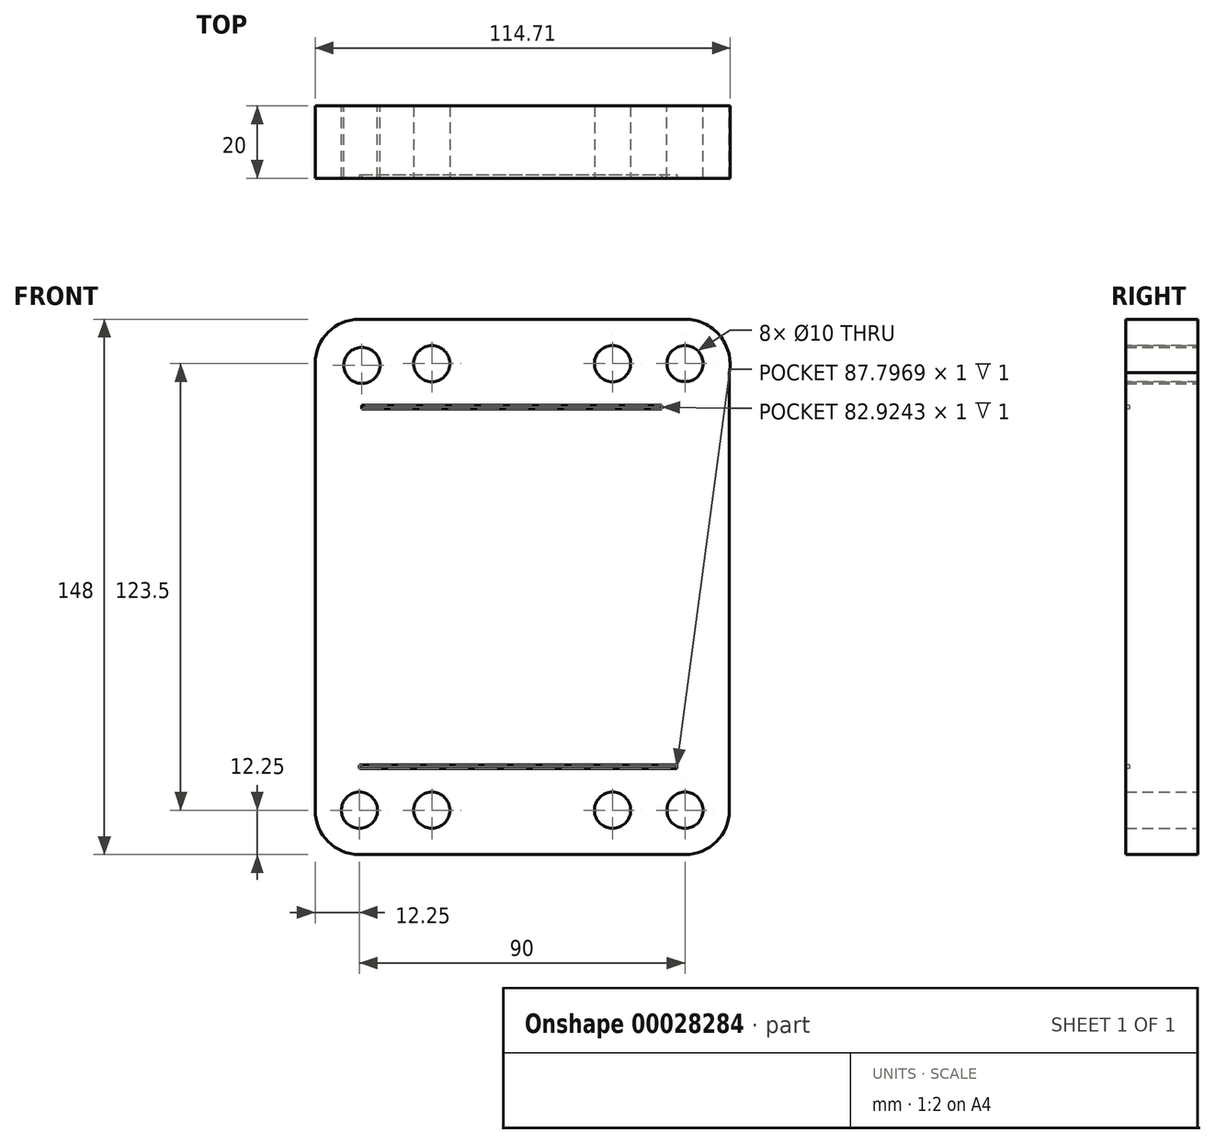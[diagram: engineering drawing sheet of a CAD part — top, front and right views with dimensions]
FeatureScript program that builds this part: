
annotation { "Feature Type Name" : "Feature", "Feature Type Description" : "" }
export const myFeature = defineFeature(function(context is Context, id is Id, definition is map)
    precondition{}
    {
        {
            var Q0;
            Q0=qCreatedBy(makeId("Front.planeOp"),FACE);
            var sketch = newSketch(context, id + "F0", { "sketchPlane" : qUnion([Q0])});
            skCircle(sketch, "E0", {"center": v(0, 0) * mm, "radius": 5 * mm});
            skCircle(sketch, "E1", {"center": v(90, 0) * mm, "radius": 5 * mm});
            skCircle(sketch, "E2", {"center": v(0.67, 123) * mm, "radius": 5 * mm});
            skCircle(sketch, "E3", {"center": v(90, 123.5) * mm, "radius": 5 * mm});
            skLineSegment(sketch, "E4.0", {"start": v(0, 135.75) * mm, "end": v(90, 135.75) * mm});
            skLineSegment(sketch, "E5.0", {"start": v(102.25, 0) * mm, "end": v(102.25, 121.01) * mm});
            skLineSegment(sketch, "E6.0", {"start": v(0, -12.25) * mm, "end": v(90, -12.25) * mm});
            skLineSegment(sketch, "E7.0", {"start": v(-12.25, 0) * mm, "end": v(-12.25, 123.5) * mm});
            skArc(sketch, "E8", {"start": v(-12.25, 123.5) * mm, "mid": v(-8.66, 132.16) * mm, "end": v(0, 135.75) * mm});
            skArc(sketch, "E9", {"start": v(90, 135.75) * mm, "mid": v(99.58, 131.25) * mm, "end": v(102.25, 121.01) * mm});
            skArc(sketch, "E10", {"start": v(102.25, 0) * mm, "mid": v(98.66, -8.66) * mm, "end": v(90, -12.25) * mm});
            skArc(sketch, "E11", {"start": v(0, -12.25) * mm, "mid": v(-8.66, -8.66) * mm, "end": v(-12.25, 0) * mm});
            skSolve(sketch);
        }
        {
            var Q0;
            Q0=makeQuery(id+"F0.imprint","IMPRINT",FACE,{"disambiguationData":[TD([[makeQuery(id+"F0.imprint","IMPRINT",EDGE,{"derivedFrom":sQuery(id+"F0.wireOp",EDGE,"E0")}),-1.0]])]});
            extrude(context, id + "F1", {"entities" : qUnion([Q0]), "depth" : 20 * mm});
        }
        {
            var Q0;
            Q0=makeQuery(id+"F1.opExtrude","CAP_FACE",FACE,{"disambiguationData":[OSD([sQuery(id+"F0.wireOp",EDGE,"E0"),sQuery(id+"F0.wireOp",EDGE,"E1"),sQuery(id+"F0.wireOp",EDGE,"E2"),sQuery(id+"F0.wireOp",EDGE,"E3"),sQuery(id+"F0.wireOp",EDGE,"E4.0"),sQuery(id+"F0.wireOp",EDGE,"E5.0"),sQuery(id+"F0.wireOp",EDGE,"E6.0"),sQuery(id+"F0.wireOp",EDGE,"E7.0"),sQuery(id+"F0.wireOp",EDGE,"E8"),sQuery(id+"F0.wireOp",EDGE,"E9"),sQuery(id+"F0.wireOp",EDGE,"E10"),sQuery(id+"F0.wireOp",EDGE,"E11")])],"isStart":false});
            var sketch = newSketch(context, id + "F2", { "sketchPlane" : qUnion([Q0])});
            skLineSegment(sketch, "E12", {"start": v(0, 12.5) * mm, "end": v(87.8, 12.5) * mm});
            skLineSegment(sketch, "E13", {"start": v(0.67, 112) * mm, "end": v(83.6, 112) * mm});
            skPoint(sketch, "E14.start.orphan", {"position": v(0.67, 123) * mm});
            skLineSegment(sketch, "E15.0", {"start": v(0, 11.5) * mm, "end": v(87.8, 11.5) * mm});
            skLineSegment(sketch, "E16.0", {"start": v(0.67, 111) * mm, "end": v(83.6, 111) * mm});
            skLineSegment(sketch, "E17", {"start": v(0.67, 112) * mm, "end": v(0.67, 111) * mm});
            skLineSegment(sketch, "E18", {"start": v(83.6, 112) * mm, "end": v(83.6, 111) * mm});
            skLineSegment(sketch, "E19", {"start": v(87.8, 12.5) * mm, "end": v(87.8, 11.5) * mm});
            skLineSegment(sketch, "E20", {"start": v(0, 12.5) * mm, "end": v(0, 11.5) * mm});
            skSolve(sketch);
        }
        {
            var Q0;
            Q0=makeQuery(id+"F2.imprint","IMPRINT",FACE,{"disambiguationData":[TD([[makeQuery(id+"F2.imprint","IMPRINT",EDGE,{"derivedFrom":sQuery(id+"F2.wireOp",EDGE,"E12")}),-1.0]])]});
            extrude(context, id + "F3", {"entities" : qUnion([Q0]), "operationType" : NewBodyOperationType.REMOVE, "oppositeDirection" : true, "depth" : 1 * mm});
        }
        {
            var Q0;
            Q0=makeQuery(id+"F2.imprint","IMPRINT",FACE,{"disambiguationData":[TD([[makeQuery(id+"F2.imprint","IMPRINT",EDGE,{"derivedFrom":sQuery(id+"F2.wireOp",EDGE,"E13")}),-1.0]])]});
            extrude(context, id + "F6", {"entities" : qUnion([Q0]), "operationType" : NewBodyOperationType.REMOVE, "oppositeDirection" : true, "depth" : 1 * mm});
        }
        {
            var Q0;
            Q0=makeQuery(id+"F2.imprint","IMPRINT",FACE,{"disambiguationData":[TD([[makeQuery(id+"F2.imprint","IMPRINT",EDGE,{"derivedFrom":sQuery(id+"F2.wireOp",EDGE,"E12")}),1.0]])]});
            var sketch = newSketch(context, id + "F4", { "sketchPlane" : qUnion([Q0])});
            skCircle(sketch, "E21", {"center": v(20, 0) * mm, "radius": 5 * mm});
            skCircle(sketch, "E22.MirrorC", {"center": v(69.97, 0) * mm, "radius": 5 * mm});
            skCircle(sketch, "E23.MirrorC", {"center": v(20, 123.48) * mm, "radius": 5 * mm});
            skCircle(sketch, "E24.MirrorC", {"center": v(69.97, 123.48) * mm, "radius": 5 * mm});
            skSolve(sketch);
        }
        {
            var Q0;
            Q0 = qSketchRegion(id + "F4", true);
            extrude(context, id + "F5", {"entities" : qUnion([Q0]), "operationType" : NewBodyOperationType.REMOVE, "oppositeDirection" : true, "depth" : 25 * mm});
        }
    });
